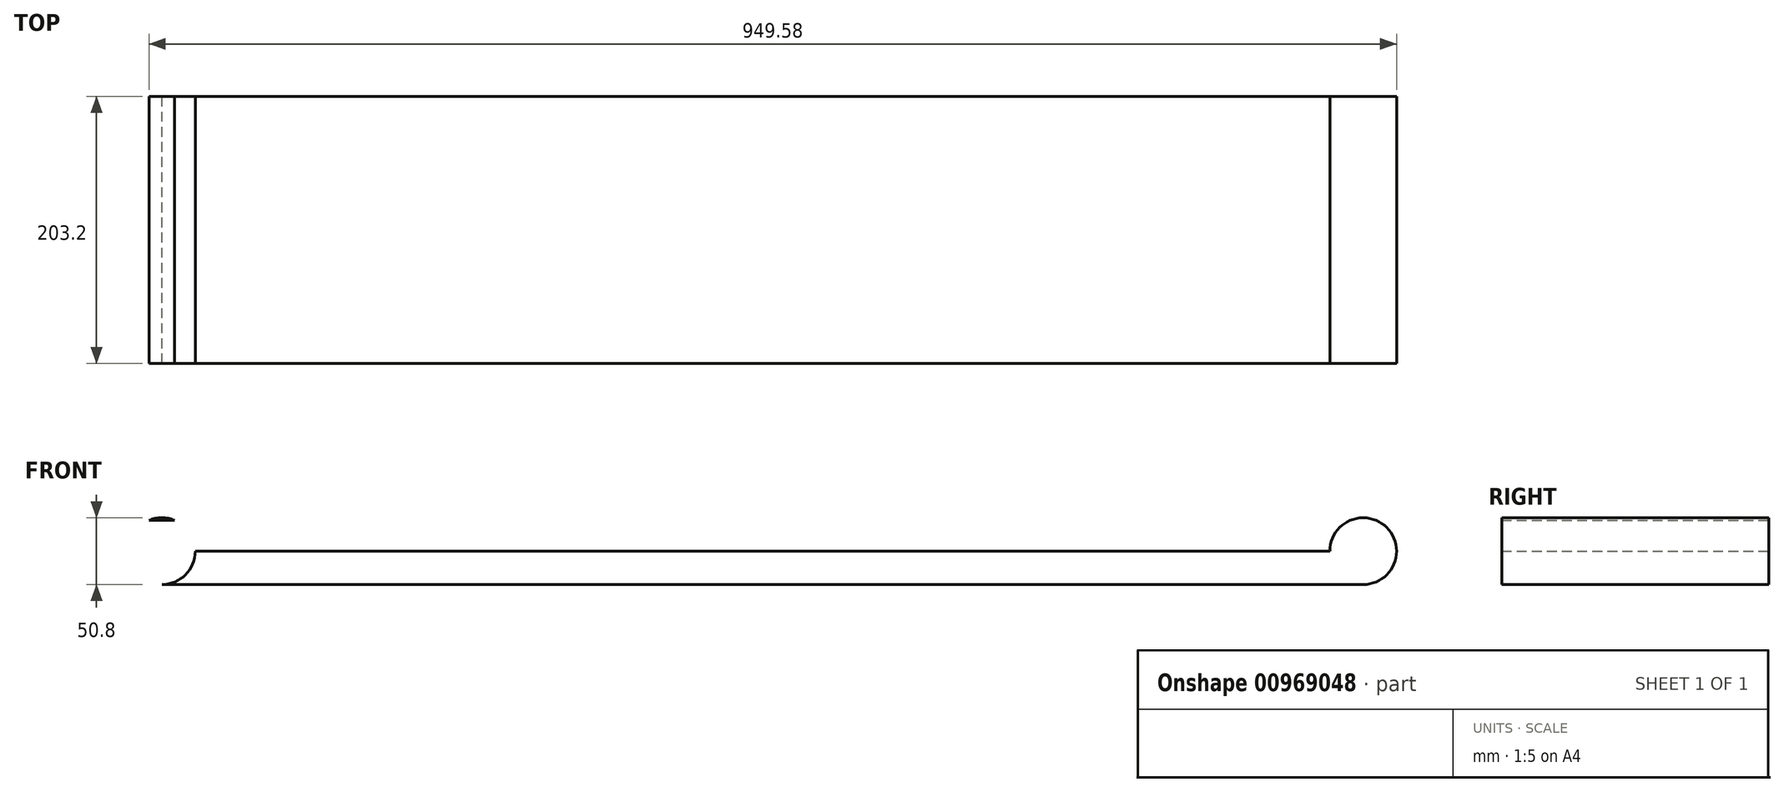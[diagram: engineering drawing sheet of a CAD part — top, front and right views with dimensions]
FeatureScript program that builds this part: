
annotation { "Feature Type Name" : "Feature", "Feature Type Description" : "" }
export const myFeature = defineFeature(function(context is Context, id is Id, definition is map)
    precondition{}
    {
        {
            var Q0;
            Q0=qCreatedBy(makeId("Front.planeOp"),FACE);
            var sketch = newSketch(context, id + "F0", { "sketchPlane" : qUnion([Q0])});
            skCircle(sketch, "E0", {"center": v(-52.45, 0) * mm, "radius": 25.4 * mm});
            skLineSegment(sketch, "E1", {"start": v(-52.45, 0) * mm, "end": v(861.95, 0) * mm});
            skCircle(sketch, "E2", {"center": v(861.95, 0) * mm, "radius": 25.4 * mm});
            skLineSegment(sketch, "E3", {"start": v(-52.45, -25.4) * mm, "end": v(862.79, -25.4) * mm});
            skLineSegment(sketch, "E4", {"start": v(-62.23, 23.44) * mm, "end": v(861.9, 25.4) * mm});
            skLineSegment(sketch, "E5", {"start": v(861.9, 25.4) * mm, "end": v(862.79, -25.4) * mm});
            skSolve(sketch);
        }
        {
            var Q0;
            {var subQ0=sQuery(id+"F0.wireOp",EDGE,"E4");var subQ1=sQuery(id+"F0.wireOp",EDGE,"E0");var subQ2=makeQuery(id+"F0.imprint","INTERSECT",VERTEX,{"disambiguationData":[OD(1.0)],"derivedFrom":[subQ1,subQ0]});Q0=makeQuery(id+"F0.imprint","IMPRINT",FACE,{"disambiguationData":[TD([[makeQuery(id+"F0.imprint","IMPRINT",EDGE,{"disambiguationData":[TD([[subQ2,1.0]])],"derivedFrom":subQ1}),1.0]])]});}
            var Q1;
            {var subQ0=sQuery(id+"F0.wireOp",EDGE,"E4");var subQ1=sQuery(id+"F0.wireOp",EDGE,"E0");var subQ2=makeQuery(id+"F0.imprint","INTERSECT",VERTEX,{"disambiguationData":[OD(1.0)],"derivedFrom":[subQ1,subQ0]});Q1=makeQuery(id+"F0.imprint","IMPRINT",FACE,{"disambiguationData":[TD([[makeQuery(id+"F0.imprint","IMPRINT",EDGE,{"disambiguationData":[TD([[subQ2,1.0]])],"derivedFrom":subQ1}),-1.0]])]});}
            var Q2;
            {var subQ0=sQuery(id+"F0.wireOp",EDGE,"E3");var subQ1=sQuery(id+"F0.wireOp",EDGE,"E0");var subQ2=makeQuery(id+"F0.imprint","INTERSECT",VERTEX,{"derivedFrom":[subQ1,subQ0]});Q2=makeQuery(id+"F0.imprint","IMPRINT",FACE,{"disambiguationData":[TD([[makeQuery(id+"F0.imprint","IMPRINT",EDGE,{"disambiguationData":[TD([[subQ2,-1.0]])],"derivedFrom":subQ1}),-1.0]])]});}
            var Q3;
            {var subQ0=sQuery(id+"F0.wireOp",EDGE,"E5");var subQ1=sQuery(id+"F0.wireOp",EDGE,"E2");var subQ3=makeQuery(id+"F0.imprint","INTERSECT",VERTEX,{"derivedFrom":[subQ1,subQ0]});Q3=makeQuery(id+"F0.imprint","IMPRINT",FACE,{"disambiguationData":[TD([[makeQuery(id+"F0.imprint","IMPRINT",EDGE,{"disambiguationData":[TD([[subQ3,-1.0]])],"derivedFrom":subQ1}),1.0]])]});}
            var Q4;
            {var subQ1=sQuery(id+"F0.wireOp",EDGE,"E2");var subQ3=makeQuery(id+"F0.imprint","INTERSECT",VERTEX,{"derivedFrom":[sQuery(id+"F0.wireOp",EDGE,"E1"),subQ1]});Q4=makeQuery(id+"F0.imprint","IMPRINT",FACE,{"disambiguationData":[TD([[makeQuery(id+"F0.imprint","IMPRINT",EDGE,{"disambiguationData":[TD([[subQ3,-1.0]])],"derivedFrom":subQ1}),1.0]])]});}
            extrude(context, id + "F1", {"entities" : qUnion([Q0, Q1, Q2, Q3, Q4]), "depth" : 203.2 * mm, "offsetDistance" : 25.4 * mm});
        }
    });
